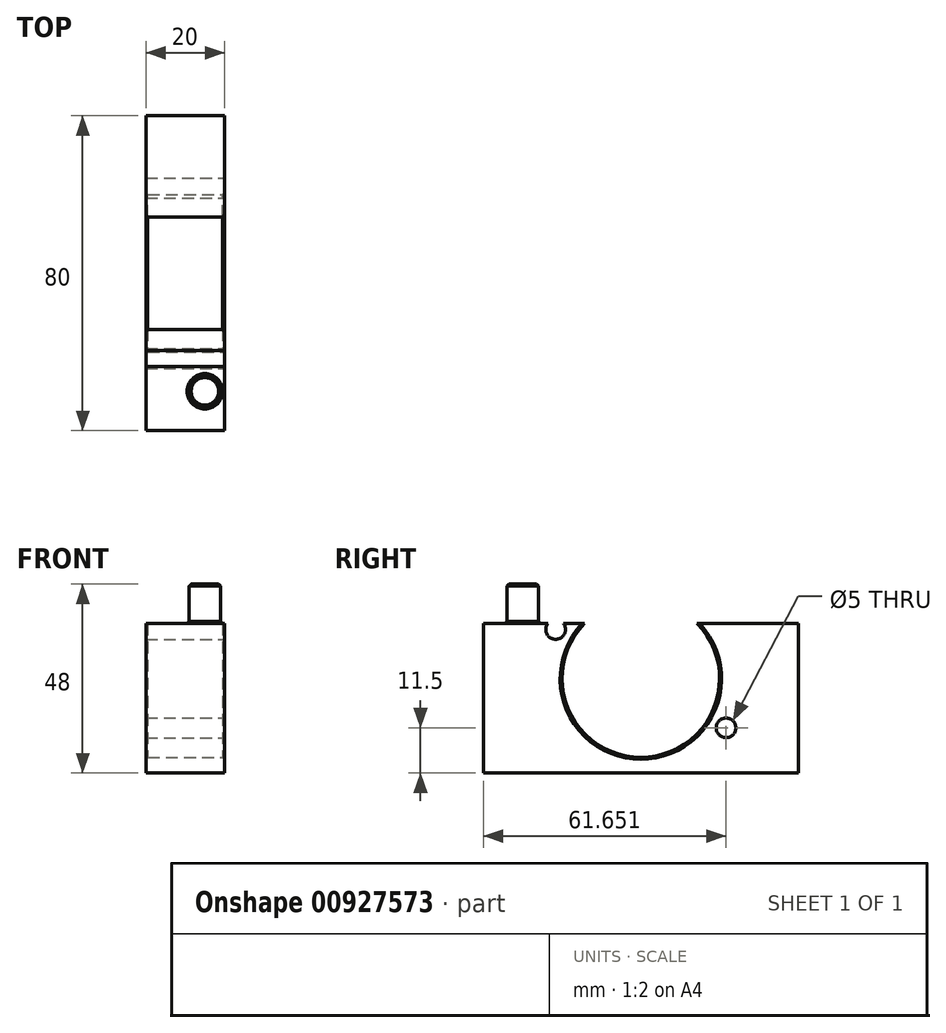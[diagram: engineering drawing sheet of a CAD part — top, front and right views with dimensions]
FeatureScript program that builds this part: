
annotation { "Feature Type Name" : "Feature", "Feature Type Description" : "" }
export const myFeature = defineFeature(function(context is Context, id is Id, definition is map)
    precondition{}
    {
        {
            var Q0;
            Q0=qCreatedBy(makeId("Right.planeOp"),FACE);
            var sketch = newSketch(context, id + "F0", { "sketchPlane" : qUnion([Q0])});
            skLineSegment(sketch, "E0.bottom", {"start": v(-40, 24) * mm, "end": v(40, 24) * mm});
            skLineSegment(sketch, "E0.top", {"start": v(-40, -24) * mm, "end": v(40, -24) * mm});
            skLineSegment(sketch, "E0.left", {"start": v(-40, 24) * mm, "end": v(-40, -24) * mm});
            skLineSegment(sketch, "E0.right", {"start": v(40, 24) * mm, "end": v(40, -24) * mm});
            skPoint(sketch, "E0.middle", {"position": v(0, 0) * mm});
            skCircle(sketch, "E1", {"center": v(0, 0) * mm, "radius": 25 * mm, "construction": true});
            skLineSegment(sketch, "E2", {"start": v(0, 0) * mm, "end": v(-33.12, -19.12) * mm, "construction": true});
            skCircle(sketch, "E3", {"center": v(0, 0) * mm, "radius": 20 * mm});
            skPoint(sketch, "E4", {"position": v(-21.65, -12.5) * mm});
            skCircle(sketch, "E5", {"center": v(-21.65, -12.5) * mm, "radius": 2.5 * mm});
            skCircle(sketch, "E6.MirrorC", {"center": v(21.65, -12.5) * mm, "radius": 2.5 * mm});
            skCircle(sketch, "E7.MirrorC", {"center": v(-21.65, 12.5) * mm, "radius": 2.5 * mm});
            skCircle(sketch, "E8.MirrorC", {"center": v(21.65, 12.5) * mm, "radius": 2.5 * mm});
            skSolve(sketch);
        }
        {
            var Q0;
            Q0=makeQuery(id+"F0.imprint","IMPRINT",FACE,{"disambiguationData":[TD([[makeQuery(id+"F0.imprint","IMPRINT",EDGE,{"derivedFrom":sQuery(id+"F0.wireOp",EDGE,"E0.bottom")}),-1.0]])]});
            var Q1;
            Q1=makeQuery(id+"F0.imprint","IMPRINT",FACE,{"disambiguationData":[TD([[makeQuery(id+"F0.imprint","IMPRINT",EDGE,{"derivedFrom":sQuery(id+"F0.wireOp",EDGE,"E7.MirrorC")}),-1.0]])]});
            var Q2;
            Q2=makeQuery(id+"F0.imprint","IMPRINT",FACE,{"disambiguationData":[TD([[makeQuery(id+"F0.imprint","IMPRINT",EDGE,{"derivedFrom":sQuery(id+"F0.wireOp",EDGE,"E5")}),1.0]])]});
            var Q3;
            Q3=makeQuery(id+"F0.imprint","IMPRINT",FACE,{"disambiguationData":[TD([[makeQuery(id+"F0.imprint","IMPRINT",EDGE,{"derivedFrom":sQuery(id+"F0.wireOp",EDGE,"E8.MirrorC")}),1.0]])]});
            var Q4;
            Q4=makeQuery(id+"F0.imprint","IMPRINT",FACE,{"disambiguationData":[TD([[makeQuery(id+"F0.imprint","IMPRINT",EDGE,{"derivedFrom":sQuery(id+"F0.wireOp",EDGE,"E6.MirrorC")}),-1.0]])]});
            extrude(context, id + "F1", {"entities" : qUnion([Q0, Q1, Q2, Q3, Q4]), "oppositeDirection" : true, "depth" : 30 * mm, "offsetDistance" : 25 * mm});
        }
        {
            var Q0;
            Q0=makeQuery(id+"F0.imprint","IMPRINT",FACE,{"disambiguationData":[TD([[makeQuery(id+"F0.imprint","IMPRINT",EDGE,{"derivedFrom":sQuery(id+"F0.wireOp",EDGE,"E7.MirrorC")}),-1.0]])]});
            var Q1;
            Q1=makeQuery(id+"F0.imprint","IMPRINT",FACE,{"disambiguationData":[TD([[makeQuery(id+"F0.imprint","IMPRINT",EDGE,{"derivedFrom":sQuery(id+"F0.wireOp",EDGE,"E8.MirrorC")}),1.0]])]});
            var Q2;
            Q2=makeQuery(id+"F0.imprint","IMPRINT",FACE,{"disambiguationData":[TD([[makeQuery(id+"F0.imprint","IMPRINT",EDGE,{"derivedFrom":sQuery(id+"F0.wireOp",EDGE,"E6.MirrorC")}),-1.0]])]});
            var Q3;
            Q3=makeQuery(id+"F0.imprint","IMPRINT",FACE,{"disambiguationData":[TD([[makeQuery(id+"F0.imprint","IMPRINT",EDGE,{"derivedFrom":sQuery(id+"F0.wireOp",EDGE,"E5")}),1.0]])]});
            extrude(context, id + "F2", {"entities" : qUnion([Q0, Q1, Q2, Q3]), "operationType" : NewBodyOperationType.REMOVE, "oppositeDirection" : true, "depth" : 10 * mm, "offsetDistance" : 25 * mm});
        }
        {
            var Q0;
            Q0=makeQuery(id+"F1.opExtrude","SWEPT_FACE",FACE,{"disambiguationData":[OSD([sQuery(id+"F0.wireOp",EDGE,"E3")])]});
            var Q1;
            Q1=makeQuery(id+"F2.boolean.opBoolean","COPY",FACE,{"derivedFrom":makeQuery(id+"F2.opExtrude","SWEPT_FACE",FACE,{"disambiguationData":[OSD([sQuery(id+"F0.wireOp",EDGE,"E7.MirrorC")])]})});
            var Q2;
            Q2=makeQuery(id+"F2.boolean.opBoolean","COPY",FACE,{"derivedFrom":makeQuery(id+"F2.opExtrude","SWEPT_FACE",FACE,{"disambiguationData":[OSD([sQuery(id+"F0.wireOp",EDGE,"E5")])]})});
            var Q3;
            Q3=makeQuery(id+"F2.boolean.opBoolean","COPY",FACE,{"derivedFrom":makeQuery(id+"F2.opExtrude","SWEPT_FACE",FACE,{"disambiguationData":[OSD([sQuery(id+"F0.wireOp",EDGE,"E8.MirrorC")])]})});
            var Q4;
            Q4=makeQuery(id+"F2.boolean.opBoolean","COPY",FACE,{"derivedFrom":makeQuery(id+"F2.opExtrude","SWEPT_FACE",FACE,{"disambiguationData":[OSD([sQuery(id+"F0.wireOp",EDGE,"E6.MirrorC")])]})});
            chamfer(context, id + "F3", {"entities" : qUnion([Q0, Q1, Q2, Q3, Q4]), "width" : 0.5 * mm, "tangentPropagation" : true});
        }
        {
            var Q0;
            Q0=makeQuery(id+"F1.opExtrude","SWEPT_FACE",FACE,{"disambiguationData":[OSD([sQuery(id+"F0.wireOp",EDGE,"E0.bottom")])]});
            var sketch = newSketch(context, id + "F4", { "sketchPlane" : qUnion([Q0])});
            skLineSegment(sketch, "E9", {"start": v(-15, 48.29) * mm, "end": v(-15, -52.25) * mm, "construction": true});
            skPoint(sketch, "E9.startSnap0", {"position": v(-15, 40) * mm});
            skCircle(sketch, "E10", {"center": v(-15, 30) * mm, "radius": 4 * mm});
            skCircle(sketch, "E11.MirrorC", {"center": v(-15, -30) * mm, "radius": 4 * mm});
            skSolve(sketch);
        }
        {
            var Q0;
            Q0=makeQuery(id+"F4.imprint","IMPRINT",FACE,{"disambiguationData":[TD([[makeQuery(id+"F4.imprint","IMPRINT",EDGE,{"derivedFrom":sQuery(id+"F4.wireOp",EDGE,"E10")}),1.0]])]});
            var Q1;
            Q1=makeQuery(id+"F4.imprint","IMPRINT",FACE,{"disambiguationData":[TD([[makeQuery(id+"F4.imprint","IMPRINT",EDGE,{"derivedFrom":sQuery(id+"F4.wireOp",EDGE,"E11.MirrorC")}),-1.0]])]});
            extrude(context, id + "F5", {"entities" : qUnion([Q0, Q1]), "operationType" : NewBodyOperationType.REMOVE, "oppositeDirection" : true, "depth" : 10 * mm, "offsetDistance" : 25 * mm});
        }
        {
            var Q0;
            Q0=makeQuery(id+"F5.boolean.opBoolean","COPY",FACE,{"derivedFrom":makeQuery(id+"F5.opExtrude","SWEPT_FACE",FACE,{"disambiguationData":[OSD([sQuery(id+"F4.wireOp",EDGE,"E10")])]})});
            var Q1;
            Q1=makeQuery(id+"F5.boolean.opBoolean","COPY",FACE,{"derivedFrom":makeQuery(id+"F5.opExtrude","SWEPT_FACE",FACE,{"disambiguationData":[OSD([sQuery(id+"F4.wireOp",EDGE,"E11.MirrorC")])]})});
            chamfer(context, id + "F6", {"entities" : qUnion([Q0, Q1]), "width" : 0.5 * mm, "tangentPropagation" : true});
        }
    });
